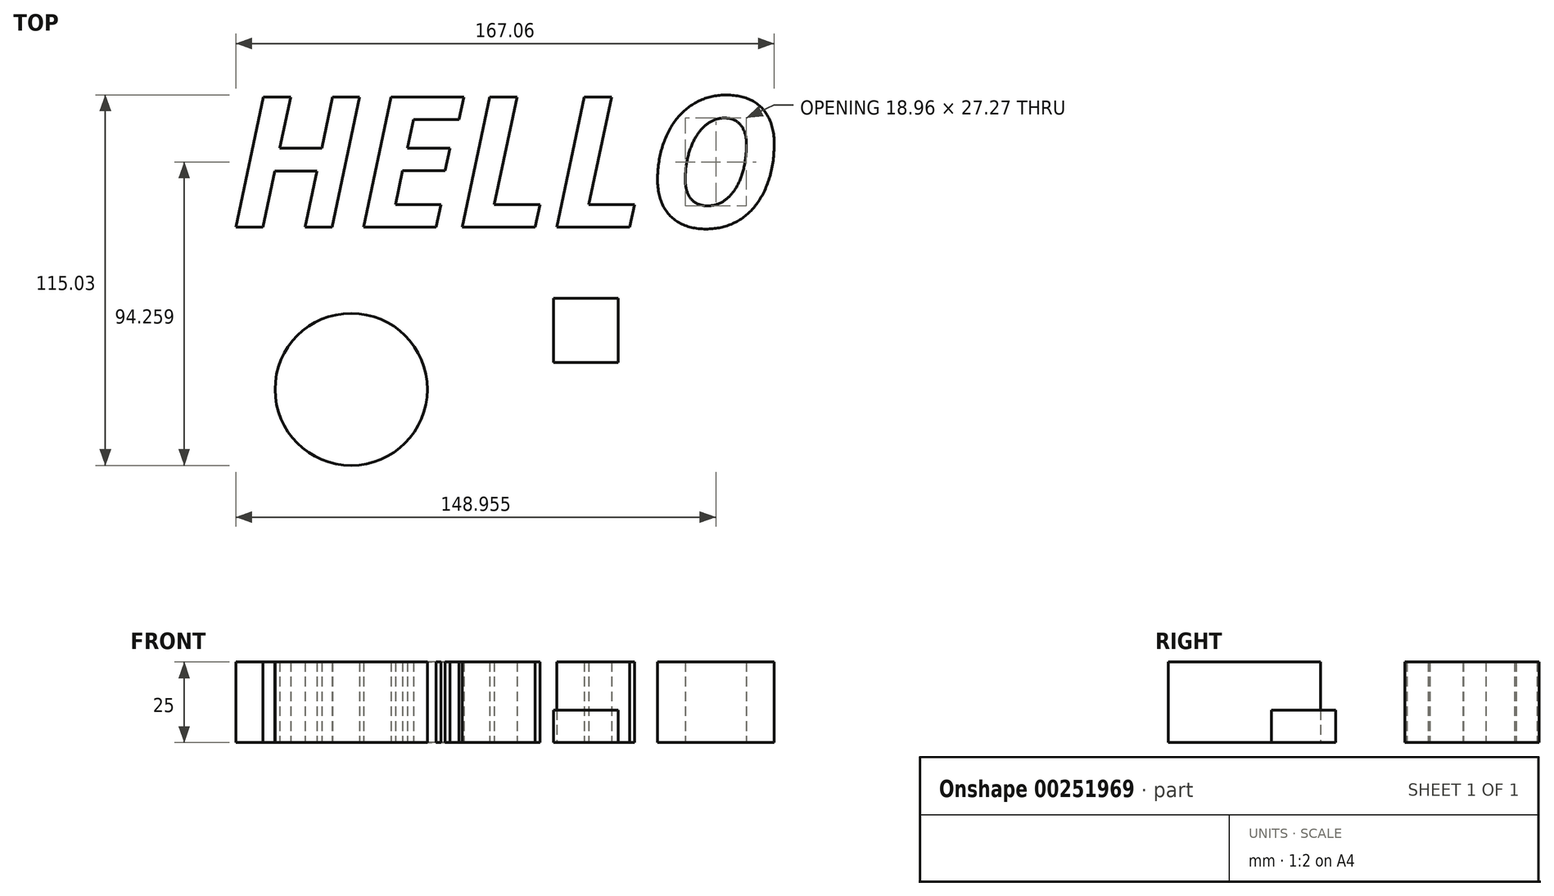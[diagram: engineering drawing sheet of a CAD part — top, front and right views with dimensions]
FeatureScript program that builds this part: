
annotation { "Feature Type Name" : "Feature", "Feature Type Description" : "" }
export const myFeature = defineFeature(function(context is Context, id is Id, definition is map)
    precondition{}
    {
        {
            var Q0;
            Q0=qCreatedBy(makeId("Front.planeOp"),FACE);
            var sketch = newSketch(context, id + "F0", { "sketchPlane" : qUnion([Q0])});
            skLineSegment(sketch, "E0.bottom", {"start": v(0, 0) * mm, "end": v(20, 0) * mm});
            skLineSegment(sketch, "E0.top", {"start": v(0, 10) * mm, "end": v(20, 10) * mm});
            skLineSegment(sketch, "E0.left", {"start": v(0, 0) * mm, "end": v(0, 10) * mm});
            skLineSegment(sketch, "E0.right", {"start": v(20, 0) * mm, "end": v(20, 10) * mm});
            skSolve(sketch);
        }
        {
            var Q0;
            Q0=makeQuery(id+"F0.imprint","IMPRINT",FACE,{"disambiguationData":[TD([[makeQuery(id+"F0.imprint","IMPRINT",EDGE,{"derivedFrom":sQuery(id+"F0.wireOp",EDGE,"E0.bottom")}),1.0]])]});
            extrude(context, id + "F1", {"entities" : qUnion([Q0]), "depth" : 20 * mm});
        }
        {
            var Q0;
            Q0=qCreatedBy(makeId("Top.planeOp"),FACE);
            var sketch = newSketch(context, id + "F2", { "sketchPlane" : qUnion([Q0])});
            skCircle(sketch, "E1", {"center": v(-62.82, -28.33) * mm, "radius": 23.62 * mm});
            skSolve(sketch);
        }
        {
            var Q0;
            Q0=makeQuery(id+"F2.imprint","IMPRINT",FACE,{"disambiguationData":[TD([[makeQuery(id+"F2.imprint","IMPRINT",EDGE,{"derivedFrom":sQuery(id+"F2.wireOp",EDGE,"E1")}),1.0]])]});
            extrude(context, id + "F3", {"entities" : qUnion([Q0]), "depth" : 25 * mm});
        }
        {
            var Q0;
            Q0=qCreatedBy(makeId("Top.planeOp"),FACE);
            var sketch = newSketch(context, id + "F4", { "sketchPlane" : qUnion([Q0])});
            skArc(sketch, "E2", {"start": v(-8.52, 51.12) * mm, "mid": v(30.42, 108.1) * mm, "end": v(-24.17, 150.33) * mm});
            skArc(sketch, "E3", {"start": v(28.23, 116.85) * mm, "mid": v(-13.87, 161.95) * mm, "end": v(-12.72, 100.26) * mm});
            skSolve(sketch);
        }
        {
            var Q0;
            Q0=sQuery(id+"F4.wireOp",EDGE,"E2");
            extrude(context, id + "F5", {"bodyType" : ToolBodyType.SURFACE, "surfaceEntities" : qUnion([Q0]), "depth" : 30 * mm});
        }
        {
            var Q0;
            Q0=qCreatedBy(makeId("Top.planeOp"),FACE);
            var sketch = newSketch(context, id + "F6", { "sketchPlane" : qUnion([Q0])});
            skText(sketch, "E4", { "text": "HELLO", "fontName": "OpenSans-BoldItalic.ttf"});
            const initialGuessF6  = {"E4": [-0.1001, 0.02203, 1, 0, 0.04075]};
            skSetInitialGuess(sketch, initialGuessF6);
            skSolve(sketch);
        }
        {
            var Q0;
            Q0 = qSketchRegion(id + "F6", true);
            extrude(context, id + "F7", {"entities" : qUnion([Q0]), "depth" : 25 * mm});
        }
    });
